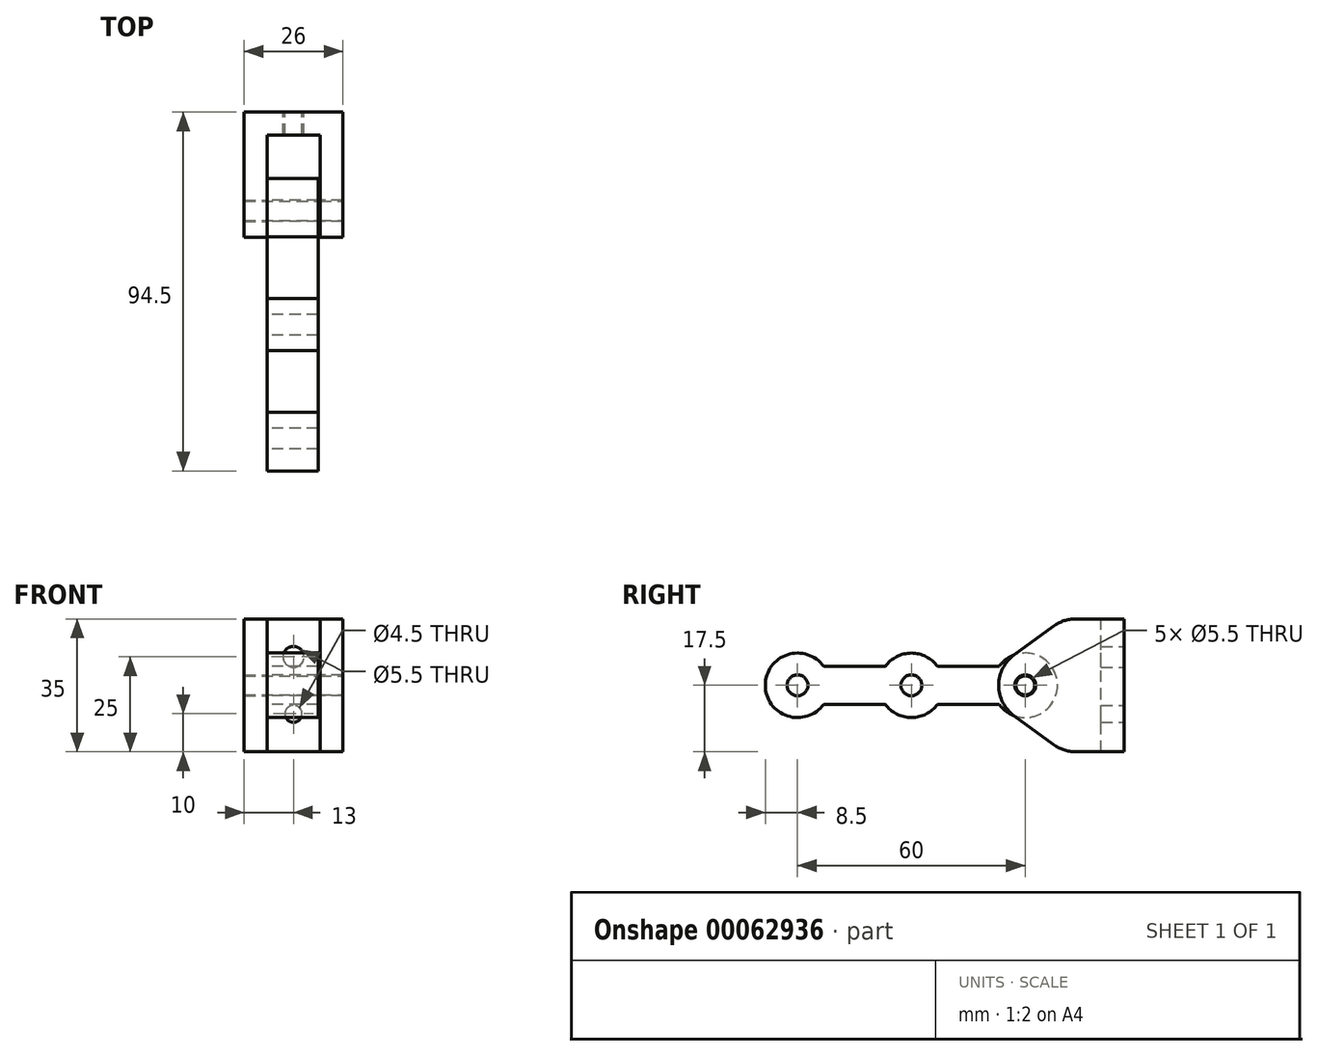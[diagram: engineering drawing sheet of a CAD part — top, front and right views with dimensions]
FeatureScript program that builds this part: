
annotation { "Feature Type Name" : "Feature", "Feature Type Description" : "" }
export const myFeature = defineFeature(function(context is Context, id is Id, definition is map)
    precondition{}
    {
        {
            var Q0;
            Q0=qCreatedBy(makeId("Front.planeOp"),FACE);
            var sketch = newSketch(context, id + "F0", { "sketchPlane" : qUnion([Q0])});
            skLineSegment(sketch, "E0.bottom", {"start": v(0, 0) * mm, "end": v(14, 0) * mm});
            skLineSegment(sketch, "E0.top", {"start": v(0, 35) * mm, "end": v(14, 35) * mm});
            skLineSegment(sketch, "E0.left", {"start": v(0, 0) * mm, "end": v(0, 35) * mm});
            skLineSegment(sketch, "E0.right", {"start": v(14, 0) * mm, "end": v(14, 35) * mm});
            skLineSegment(sketch, "E1", {"start": v(7, 0) * mm, "end": v(7, 35) * mm, "construction": true});
            skCircle(sketch, "E2", {"center": v(7, 10) * mm, "radius": 2.25 * mm});
            skCircle(sketch, "E3", {"center": v(7, 25) * mm, "radius": 2.75 * mm});
            skSolve(sketch);
        }
        {
            var Q0;
            Q0 = qSketchRegion(id + "F0", true);
            extrude(context, id + "F1", {"entities" : qUnion([Q0]), "depth" : 6 * mm});
        }
        {
            var Q0;
            Q0=makeQuery(id+"F1.opExtrude","SWEPT_FACE",FACE,{"disambiguationData":[OSD([sQuery(id+"F0.wireOp",EDGE,"E0.right")])]});
            var sketch = newSketch(context, id + "F2", { "sketchPlane" : qUnion([Q0])});
            skLineSegment(sketch, "E4", {"start": v(0, 35) * mm, "end": v(-12.69, 35) * mm});
            skLineSegment(sketch, "E5", {"start": v(-18.57, 33.09) * mm, "end": v(-28.88, 25.59) * mm});
            skLineSegment(sketch, "E6", {"start": v(-28.88, 9.41) * mm, "end": v(-18.57, 1.91) * mm});
            skLineSegment(sketch, "E7", {"start": v(-12.69, 0) * mm, "end": v(0, 0) * mm});
            skPoint(sketch, "E8.visualSharp", {"position": v(-40, 17.5) * mm});
            skArc(sketch, "E8.filletArc", {"start": v(-28.88, 25.59) * mm, "mid": v(-33, 17.5) * mm, "end": v(-28.88, 9.41) * mm});
            skPoint(sketch, "E9.visualSharp", {"position": v(-15.94, 35) * mm});
            skArc(sketch, "E9.filletArc", {"start": v(-12.69, 35) * mm, "mid": v(-15.78, 34.5) * mm, "end": v(-18.57, 33.09) * mm});
            skPoint(sketch, "E10.visualSharp", {"position": v(-15.94, 0) * mm});
            skArc(sketch, "E10.filletArc", {"start": v(-18.57, 1.91) * mm, "mid": v(-15.78, 0.5) * mm, "end": v(-12.69, 0) * mm});
            skLineSegment(sketch, "E11", {"start": v(-40, 17.5) * mm, "end": v(0, 17.5) * mm, "construction": true});
            skCircle(sketch, "E12", {"center": v(-26, 17.5) * mm, "radius": 2.75 * mm});
            skPoint(sketch, "E13", {"position": v(-20, 17.5) * mm});
            skSolve(sketch);
        }
        {
            var Q0;
            Q0=makeQuery(id+"F2.imprint","IMPRINT",FACE,{"disambiguationData":[TD([[makeQuery(id+"F2.imprint","IMPRINT",EDGE,{"derivedFrom":sQuery(id+"F2.wireOp",EDGE,"E5")}),1.0]])]});
            var Q1;
            {var subQ1=sQuery(id+"F0.wireOp",EDGE,"E0.right");var subQ2=makeQuery(id+"F1.opExtrude","CAP_EDGE",EDGE,{"disambiguationData":[OSD([subQ1])],"isStart":true});Q1=makeQuery(id+"F2.imprint","IMPRINT",FACE,{"disambiguationData":[TD([[makeQuery(id+"F2.imprint","IMPRINT",EDGE,{"derivedFrom":subQ2}),1.0]])]});}
            extrude(context, id + "F3", {"entities" : qUnion([Q0, Q1]), "operationType" : NewBodyOperationType.ADD, "depth" : 6 * mm});
        }
        {
            var Q0;
            Q0=makeQuery(id+"F1.opExtrude","SWEPT_FACE",FACE,{"disambiguationData":[OSD([sQuery(id+"F0.wireOp",EDGE,"E0.left")])]});
            var sketch = newSketch(context, id + "F4", { "sketchPlane" : qUnion([Q0])});
            skLineSegment(sketch, "E14", {"start": v(0, 35) * mm, "end": v(0, 0) * mm});
            skPoint(sketch, "E15.visualSharp", {"position": v(67.57, 12.5) * mm});
            skLineSegment(sketch, "E16", {"start": v(0, 35) * mm, "end": v(12.69, 35) * mm});
            skLineSegment(sketch, "E17", {"start": v(0, 0) * mm, "end": v(12.69, 0) * mm});
            skLineSegment(sketch, "E18", {"start": v(0, 17.5) * mm, "end": v(35, 17.5) * mm, "construction": true});
            skLineSegment(sketch, "E19", {"start": v(18.57, 33.09) * mm, "end": v(28.88, 25.59) * mm});
            skLineSegment(sketch, "E20", {"start": v(28.88, 9.41) * mm, "end": v(18.57, 1.91) * mm});
            skPoint(sketch, "E21.visualSharp", {"position": v(40, 17.5) * mm});
            skArc(sketch, "E21.filletArc", {"start": v(28.88, 9.41) * mm, "mid": v(33, 17.5) * mm, "end": v(28.88, 25.59) * mm});
            skPoint(sketch, "E22.visualSharp", {"position": v(15.94, 35) * mm});
            skArc(sketch, "E22.filletArc", {"start": v(18.57, 33.09) * mm, "mid": v(15.78, 34.5) * mm, "end": v(12.69, 35) * mm});
            skPoint(sketch, "E23.visualSharp", {"position": v(15.94, 0) * mm});
            skArc(sketch, "E23.filletArc", {"start": v(12.69, 0) * mm, "mid": v(15.78, 0.5) * mm, "end": v(18.57, 1.91) * mm});
            skCircle(sketch, "E24", {"center": v(26, 17.5) * mm, "radius": 2.75 * mm});
            skSolve(sketch);
        }
        {
            var Q0;
            Q0=makeQuery(id+"F4.imprint","IMPRINT",FACE,{"disambiguationData":[TD([[makeQuery(id+"F4.imprint","IMPRINT",EDGE,{"derivedFrom":sQuery(id+"F4.wireOp",EDGE,"E19")}),-1.0]])]});
            var Q1;
            {var subQ0=sQuery(id+"F4.wireOp",EDGE,"E14");Q1=makeQuery(id+"F4.imprint","IMPRINT",FACE,{"disambiguationData":[TD([[makeQuery(id+"F4.imprint","IMPRINT",EDGE,{"derivedFrom":subQ0}),-1.0]])]});}
            extrude(context, id + "F5", {"entities" : qUnion([Q0, Q1]), "operationType" : NewBodyOperationType.ADD, "depth" : 6 * mm});
        }
        {
            var Q0;
            Q0=makeQuery(id+"F3.opExtrude","CAP_FACE",FACE,{"disambiguationData":[OSD([sQuery(id+"F0.wireOp",EDGE,"E0.right"),sQuery(id+"F2.wireOp",EDGE,"E4"),sQuery(id+"F2.wireOp",EDGE,"E5"),sQuery(id+"F2.wireOp",EDGE,"E6"),sQuery(id+"F2.wireOp",EDGE,"E7"),sQuery(id+"F2.wireOp",EDGE,"E8.filletArc"),sQuery(id+"F2.wireOp",EDGE,"E9.filletArc"),sQuery(id+"F2.wireOp",EDGE,"E10.filletArc"),sQuery(id+"F2.wireOp",EDGE,"E12")])],"isStart":false});
            var sketch = newSketch(context, id + "F6", { "sketchPlane" : qUnion([Q0])});
            skCircle(sketch, "E25", {"center": v(-26, 17.5) * mm, "radius": 2.5 * mm});
            skSolve(sketch);
        }
        {
            var Q0;
            Q0=makeQuery(id+"F6.imprint","IMPRINT",FACE,{"disambiguationData":[TD([[makeQuery(id+"F6.imprint","IMPRINT",EDGE,{"derivedFrom":sQuery(id+"F6.wireOp",EDGE,"E25")}),1.0]])]});
            extrude(context, id + "F7", {"entities" : qUnion([Q0]), "oppositeDirection" : true, "depth" : 26 * mm});
        }
        {
            var Q0;
            Q0=makeQuery(id+"F5.opExtrude","CAP_FACE",FACE,{"disambiguationData":[OSD([sQuery(id+"F4.wireOp",EDGE,"E14"),sQuery(id+"F4.wireOp",EDGE,"E16"),sQuery(id+"F4.wireOp",EDGE,"E17"),sQuery(id+"F4.wireOp",EDGE,"E19"),sQuery(id+"F4.wireOp",EDGE,"E20"),sQuery(id+"F4.wireOp",EDGE,"E21.filletArc"),sQuery(id+"F4.wireOp",EDGE,"E22.filletArc"),sQuery(id+"F4.wireOp",EDGE,"E23.filletArc"),sQuery(id+"F4.wireOp",EDGE,"E24")])],"isStart":true});
            var sketch = newSketch(context, id + "F8", { "sketchPlane" : qUnion([Q0])});
            skArc(sketch, "E26", {"start": v(-32.87, 12.5) * mm, "mid": v(-17.5, 17.5) * mm, "end": v(-32.87, 22.5) * mm});
            skArc(sketch, "E27", {"start": v(-79.13, 22.5) * mm, "mid": v(-94.5, 17.5) * mm, "end": v(-79.13, 12.5) * mm});
            skLineSegment(sketch, "E28", {"start": v(-79.13, 12.5) * mm, "end": v(-62.87, 12.5) * mm});
            skLineSegment(sketch, "E29", {"start": v(-32.87, 22.5) * mm, "end": v(-49.13, 22.5) * mm});
            skLineSegment(sketch, "E30", {"start": v(-86, 17.5) * mm, "end": v(-26, 17.5) * mm, "construction": true});
            skArc(sketch, "E31", {"start": v(-62.87, 12.5) * mm, "mid": v(-56, 9) * mm, "end": v(-49.13, 12.5) * mm});
            skCircle(sketch, "E32", {"center": v(-86, 17.5) * mm, "radius": 2.75 * mm});
            skCircle(sketch, "E33", {"center": v(-56, 17.5) * mm, "radius": 2.75 * mm});
            skCircle(sketch, "E34", {"center": v(-26, 17.5) * mm, "radius": 2.75 * mm});
            skArc(sketch, "E35.trimOffspring", {"start": v(-49.13, 22.5) * mm, "mid": v(-56, 26) * mm, "end": v(-62.87, 22.5) * mm});
            skLineSegment(sketch, "E36.trimOffspring", {"start": v(-49.13, 12.5) * mm, "end": v(-32.87, 12.5) * mm});
            skLineSegment(sketch, "E37.trimOffspring", {"start": v(-62.87, 22.5) * mm, "end": v(-79.13, 22.5) * mm});
            skSolve(sketch);
        }
        {
            var Q0;
            Q0 = qSketchRegion(id + "F8", true);
            extrude(context, id + "F9", {"entities" : qUnion([Q0]), "depth" : 13.5 * mm});
        }
    });
